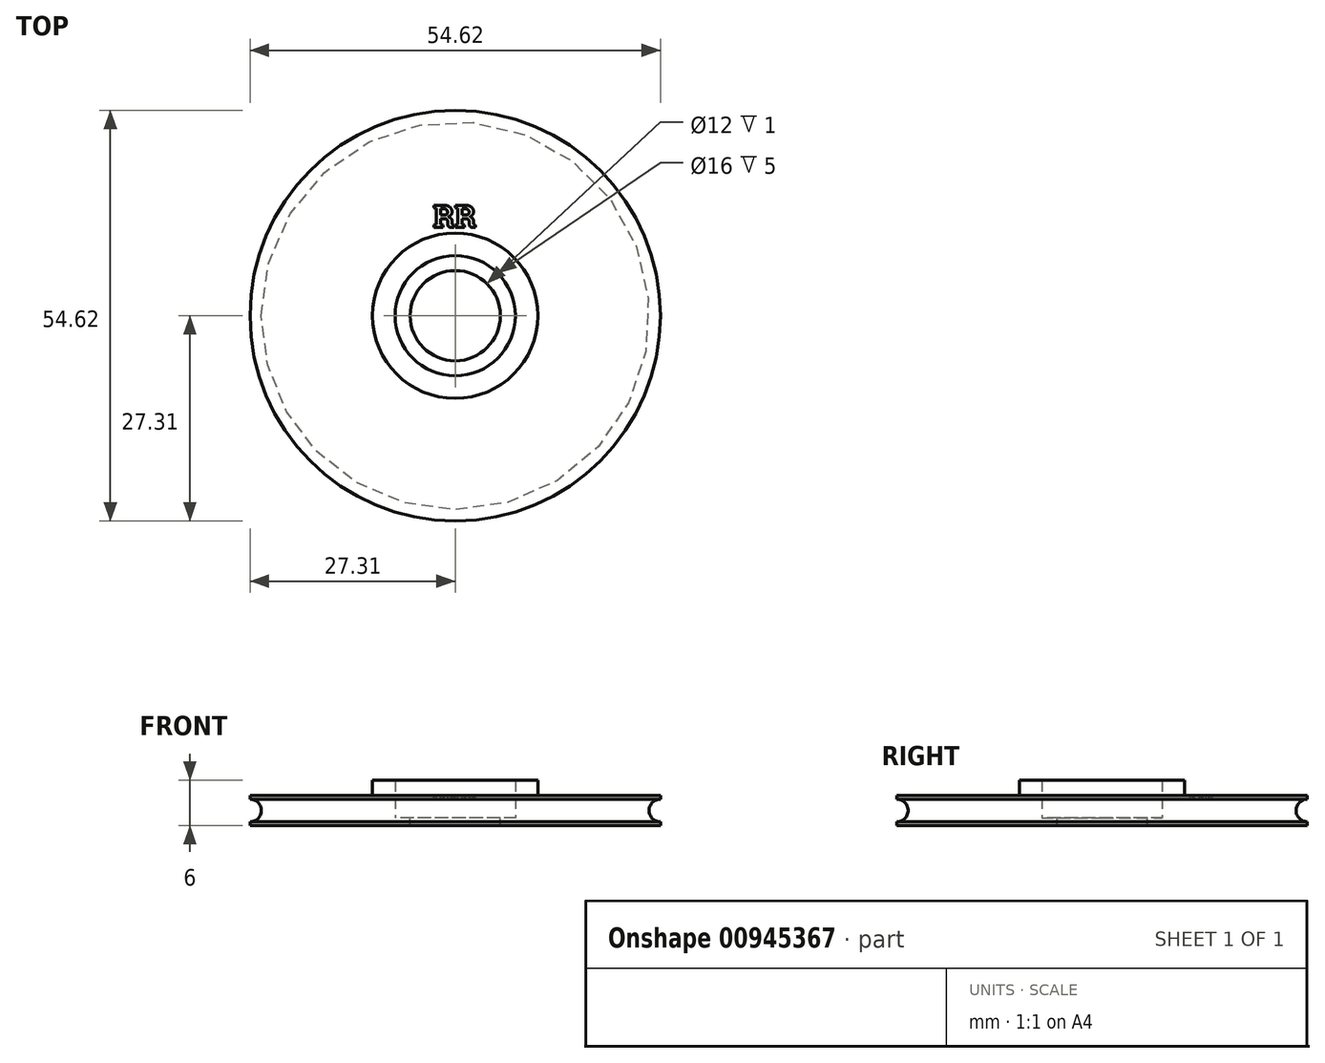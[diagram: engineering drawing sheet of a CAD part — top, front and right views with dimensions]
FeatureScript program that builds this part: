
annotation { "Feature Type Name" : "Feature", "Feature Type Description" : "" }
export const myFeature = defineFeature(function(context is Context, id is Id, definition is map)
    precondition{}
    {
        {
            var Q0;
            Q0=qCreatedBy(makeId("Top.planeOp"),FACE);
            var sketch = newSketch(context, id + "F0", { "sketchPlane" : qUnion([Q0])});
            skCircle(sketch, "E0", {"center": v(0, 0) * mm, "radius": 27.3 * mm});
            skSolve(sketch);
        }
        {
            var Q0;
            Q0=makeQuery(id+"F0.imprint","IMPRINT",FACE,{"disambiguationData":[TD([[makeQuery(id+"F0.imprint","IMPRINT",EDGE,{"derivedFrom":sQuery(id+"F0.wireOp",EDGE,"E0")}),1.0]])]});
            extrude(context, id + "F1", {"entities" : qUnion([Q0]), "depth" : 4 * mm, "offsetDistance" : 25.4 * mm});
        }
        {
            var Q0;
            Q0=makeQuery(id+"F1.opExtrude","CAP_FACE",FACE,{"disambiguationData":[OSD([sQuery(id+"F0.wireOp",EDGE,"E0"),sQuery(id+"F0.wireOp",EDGE,"n39IqKt5-bk1q-LU1x-fgod-8OyBNiFTd7FZ")])],"isStart":false});
            var sketch = newSketch(context, id + "F2", { "sketchPlane" : qUnion([Q0])});
            skCircle(sketch, "E1", {"center": v(0, 0) * mm, "radius": 8 * mm});
            skCircle(sketch, "E2.0", {"center": v(0, 0) * mm, "radius": 11 * mm});
            skSolve(sketch);
        }
        {
            var Q0;
            Q0=qSketchRegion(id+"F2",true);
            extrude(context, id + "F3", {"entities" : qUnion([Q0]), "operationType" : NewBodyOperationType.ADD, "depth" : 2 * mm, "offsetDistance" : 25.4 * mm});
        }
        {
            var Q0;
            Q0=makeQuery(id+"F3.boolean.opBoolean","SPLIT",FACE,{"disambiguationData":[TD([makeQuery(id+"F3.opExtrude","SWEPT_FACE",FACE,{"disambiguationData":[OSD([sQuery(id+"F2.wireOp",EDGE,"E1")])]})])],"derivedFrom":makeQuery(id+"F1.opExtrude","CAP_FACE",FACE,{"disambiguationData":[OSD([sQuery(id+"F0.wireOp",EDGE,"E0")])],"isStart":false})});
            var sketch = newSketch(context, id + "F4", { "sketchPlane" : qUnion([Q0])});
            skCircle(sketch, "E3", {"center": v(0, 0) * mm, "radius": 6 * mm});
            skSolve(sketch);
        }
        {
            var Q0;
            Q0=makeQuery(id+"F4.imprint","IMPRINT",FACE,{"disambiguationData":[TD([[makeQuery(id+"F4.imprint","IMPRINT",EDGE,{"derivedFrom":sQuery(id+"F4.wireOp",EDGE,"E3")}),1.0]])]});
            var Q1;
            Q1=makeQuery(id+"F4.imprint","IMPRINT",FACE,{"disambiguationData":[TD([[makeQuery(id+"F4.imprint","IMPRINT",EDGE,{"derivedFrom":makeQuery(id+"FgYK8jIepfClWtA_1.opExtrude","CAP_EDGE",EDGE,{"disambiguationData":[OSD([sQuery(id+"F8DXjnVyigKkjng_1.wireOp",EDGE,"EUjAMsCd-Zx2B-3j4q-cP5o-T3GrjTijNDqK")])],"isStart":false})}),1.0]])]});
            extrude(context, id + "F5", {"entities" : qUnion([Q0, Q1]), "operationType" : NewBodyOperationType.REMOVE, "oppositeDirection" : true, "depth" : 9 * mm, "offsetDistance" : 25.4 * mm});
        }
        {
            var Q0;
            Q0=qCreatedBy(makeId("Front.planeOp"),FACE);
            var sketch = newSketch(context, id + "F6", { "sketchPlane" : qUnion([Q0])});
            skCircle(sketch, "E4", {"center": v(-27.3, 2) * mm, "radius": 1.5 * mm});
            skLineSegment(sketch, "E5.bottom", {"start": v(-25.8, 0.65) * mm, "end": v(-27.95, 0.65) * mm});
            skLineSegment(sketch, "E5.top", {"start": v(-25.8, 3.35) * mm, "end": v(-27.95, 3.35) * mm});
            skLineSegment(sketch, "E5.left", {"start": v(-25.8, 0.65) * mm, "end": v(-25.8, 3.35) * mm});
            skLineSegment(sketch, "E5.right", {"start": v(-28.8, 1.91) * mm, "end": v(-28.8, 2.09) * mm});
            skLineSegment(sketch, "E6", {"start": v(0, 19.1) * mm, "end": v(0, -12.61) * mm, "construction": true});
            skLineSegment(sketch, "E7", {"start": v(-25.8, 1.83) * mm, "end": v(-25.81, 1.83) * mm});
            skPoint(sketch, "E8.orphan", {"position": v(-38.97, 3.35) * mm});
            skPoint(sketch, "E9.end.orphan", {"position": v(-15.64, 0.65) * mm});
            skPoint(sketch, "E9.start.orphan", {"position": v(-25.8, 2) * mm});
            skSolve(sketch);
        }
        {
            var Q0;
            {var subQ0=sQuery(id+"F6.wireOp",EDGE,"E5.top");var subQ1=sQuery(id+"F6.wireOp",EDGE,"E4");var subQ2=makeQuery(id+"F6.imprint","INTERSECT",VERTEX,{"disambiguationData":[OD(0.0)],"derivedFrom":[subQ1,subQ0]});Q0=makeQuery(id+"F6.imprint","IMPRINT",FACE,{"disambiguationData":[TD([[makeQuery(id+"F6.imprint","IMPRINT",EDGE,{"disambiguationData":[TD([[subQ2,1.0]])],"derivedFrom":subQ1}),1.0]])]});}
            var Q1;
            {var subQ0=sQuery(id+"F6.wireOp",EDGE,"E5.bottom");var subQ1=sQuery(id+"F6.wireOp",EDGE,"E4");var subQ2=makeQuery(id+"F6.imprint","INTERSECT",VERTEX,{"disambiguationData":[OD(0.0)],"derivedFrom":[subQ1,subQ0]});Q1=makeQuery(id+"F6.imprint","IMPRINT",FACE,{"disambiguationData":[TD([[makeQuery(id+"F6.imprint","IMPRINT",EDGE,{"disambiguationData":[TD([[subQ2,-1.0]])],"derivedFrom":subQ1}),1.0]])]});}
            var Q2;
            {var subQ4=sQuery(id+"F6.wireOp",EDGE,"E5.right");Q2=makeQuery(id+"F6.imprint","IMPRINT",FACE,{"disambiguationData":[TD([[makeQuery(id+"F6.imprint","IMPRINT",EDGE,{"derivedFrom":subQ4}),-1.0]])]});}
            var Q3;
            {var subQ0=sQuery(id+"F6.wireOp",EDGE,"p3G3spWP-JurA-dj01-Cwvm-HHlCDoPDIoxd");Q3=makeQuery(id+"F6.imprint","IMPRINT",FACE,{"disambiguationData":[TD([[makeQuery(id+"F6.imprint","IMPRINT",EDGE,{"derivedFrom":subQ0}),1.0]])]});}
            var Q4;
            Q4=makeQuery(id+"F6.imprint","IMPRINT",FACE,{"disambiguationData":[TD([[makeQuery(id+"F6.imprint","IMPRINT",EDGE,{"derivedFrom":sQuery(id+"F6.wireOp",EDGE,"p3G3spWP-JurA-dj01-Cwvm-HHlCDoPDIoxd")}),-1.0]])]});
            var Q5;
            {var subQ0=sQuery(id+"F6.wireOp",EDGE,"E9");Q5=makeQuery(id+"F6.imprint","IMPRINT",FACE,{"disambiguationData":[TD([[makeQuery(id+"F6.imprint","IMPRINT",EDGE,{"derivedFrom":subQ0}),1.0]])]});}
            var Q6;
            Q6=sQuery(id+"F6.wireOp",EDGE,"E6");
            revolve(context, id + "F7", {"operationType" : NewBodyOperationType.REMOVE, "surfaceOperationType" : NewSurfaceOperationType.NEW, "entities" : qUnion([Q0, Q1, Q2, Q3, Q4, Q5]), "axis" : qUnion([Q6]), "revolveType" : RevolveType.FULL, "oppositeDirection" : true});
        }
        {
            var Q0;
            Q0=makeQuery(id+"F3.boolean.opBoolean","SPLIT",FACE,{"disambiguationData":[TD([makeQuery(id+"F3.opExtrude","SWEPT_FACE",FACE,{"disambiguationData":[OSD([sQuery(id+"F2.wireOp",EDGE,"E1")])]})])],"derivedFrom":makeQuery(id+"F1.opExtrude","CAP_FACE",FACE,{"disambiguationData":[OSD([sQuery(id+"F0.wireOp",EDGE,"E0")])],"isStart":false})});
            extrude(context, id + "F8", {"entities" : qUnion([Q0]), "operationType" : NewBodyOperationType.REMOVE, "oppositeDirection" : true, "depth" : 3 * mm, "offsetDistance" : 25 * mm});
        }
        {
            var Q0;
            {var subQ0=sQuery(id+"F0.wireOp",EDGE,"E0");Q0=makeQuery(id+"F3.boolean.opBoolean","SPLIT",FACE,{"disambiguationData":[TD([makeQuery(id+"F1.opExtrude","SWEPT_FACE",FACE,{"disambiguationData":[OSD([subQ0])]})])],"derivedFrom":makeQuery(id+"F1.opExtrude","CAP_FACE",FACE,{"disambiguationData":[OSD([subQ0])],"isStart":false})});}
            var sketch = newSketch(context, id + "F9", { "sketchPlane" : qUnion([Q0])});
            skText(sketch, "E10", { "text": "RR", "fontName": "RobotoSlab-Bold.ttf"});
            const initialGuessF9  = {"E10": [-0.00295, 0.01172, 1, 0, 0.003]};
            skSetInitialGuess(sketch, initialGuessF9);
            skSolve(sketch);
        }
        {
            var Q0;
            Q0 = qSketchRegion(id + "F9", true);
            extrude(context, id + "F10", {"entities" : qUnion([Q0]), "operationType" : NewBodyOperationType.REMOVE, "oppositeDirection" : true, "depth" : .5 * mm, "offsetDistance" : 25 * mm});
        }
    });
